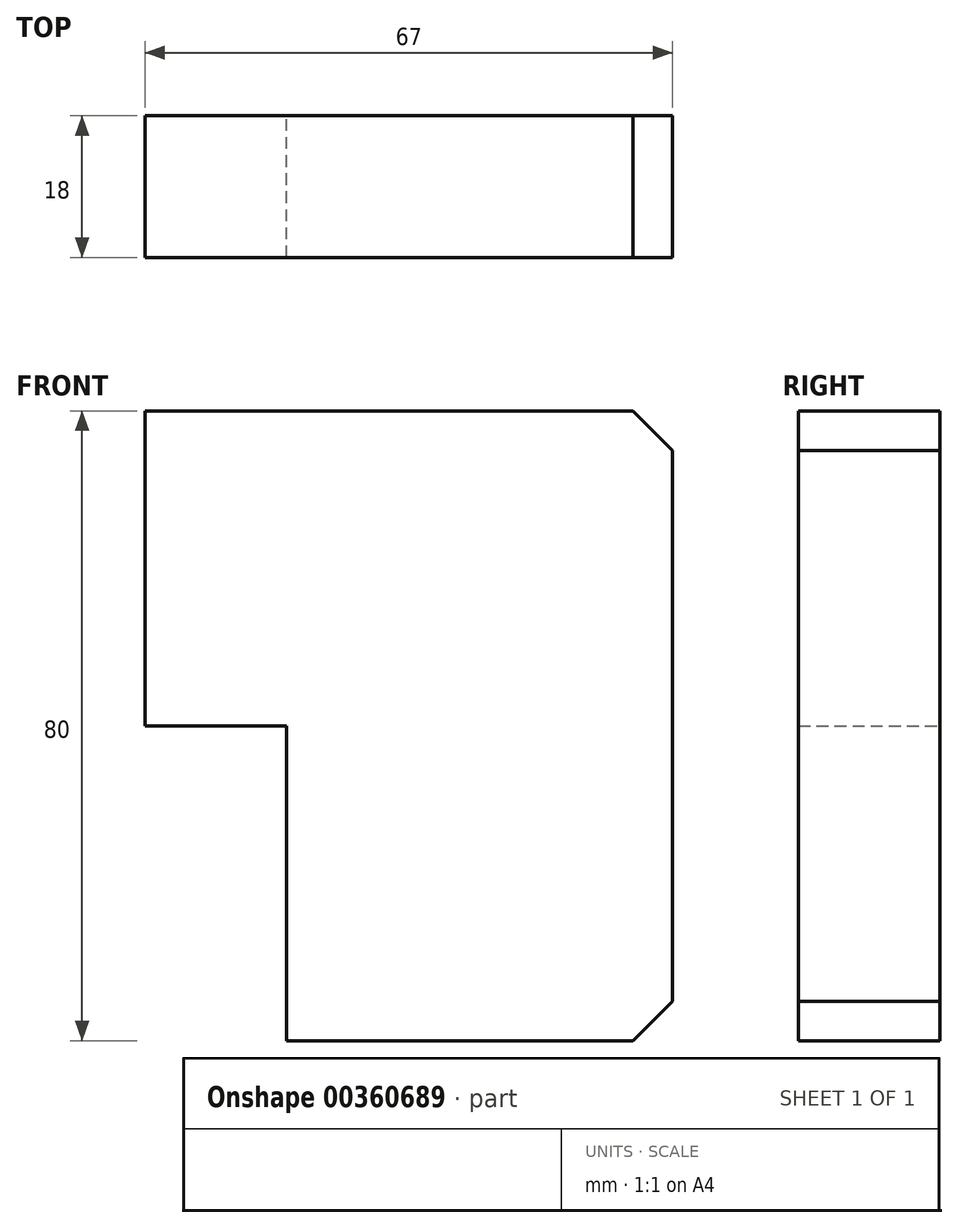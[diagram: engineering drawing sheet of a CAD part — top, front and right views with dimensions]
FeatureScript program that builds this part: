
annotation { "Feature Type Name" : "Feature", "Feature Type Description" : "" }
export const myFeature = defineFeature(function(context is Context, id is Id, definition is map)
    precondition{}
    {
        {
            var Q0;
            Q0=qCreatedBy(makeId("Front.planeOp"),FACE);
            var sketch = newSketch(context, id + "F0", { "sketchPlane" : qUnion([Q0])});
            skLineSegment(sketch, "E0.bottom", {"start": v(18, 0) * mm, "end": v(67, 0) * mm});
            skLineSegment(sketch, "E0.top", {"start": v(0, 80) * mm, "end": v(67, 80) * mm});
            skLineSegment(sketch, "E0.left", {"start": v(0, 40) * mm, "end": v(0, 80) * mm});
            skLineSegment(sketch, "E0.right", {"start": v(67, 0) * mm, "end": v(67, 80) * mm});
            skLineSegment(sketch, "E1.top", {"start": v(0, 40) * mm, "end": v(18, 40) * mm});
            skLineSegment(sketch, "E1.right", {"start": v(18, 0) * mm, "end": v(18, 40) * mm});
            skSolve(sketch);
        }
        {
            var Q0;
            Q0=makeQuery(id+"F0.imprint","IMPRINT",FACE,{"disambiguationData":[TD([[makeQuery(id+"F0.imprint","IMPRINT",EDGE,{"derivedFrom":sQuery(id+"F0.wireOp",EDGE,"E0.bottom")}),1.0]])]});
            extrude(context, id + "F1", {"entities" : qUnion([Q0]), "depth" : 18 * mm});
        }
        {
            var Q0;
            Q0=makeQuery(id+"F1.opExtrude","SWEPT_EDGE",EDGE,{"disambiguationData":[OSD([sQuery(id+"F0.wireOp",EDGE,"E0.top"),sQuery(id+"F0.wireOp",EDGE,"E0.right")])]});
            var Q1;
            Q1=makeQuery(id+"F1.opExtrude","SWEPT_EDGE",EDGE,{"disambiguationData":[OSD([sQuery(id+"F0.wireOp",EDGE,"E0.bottom"),sQuery(id+"F0.wireOp",EDGE,"E0.right")])]});
            chamfer(context, id + "F2", {"entities" : qUnion([Q0, Q1]), "width" : 5 * mm, "tangentPropagation" : true});
        }
    });
